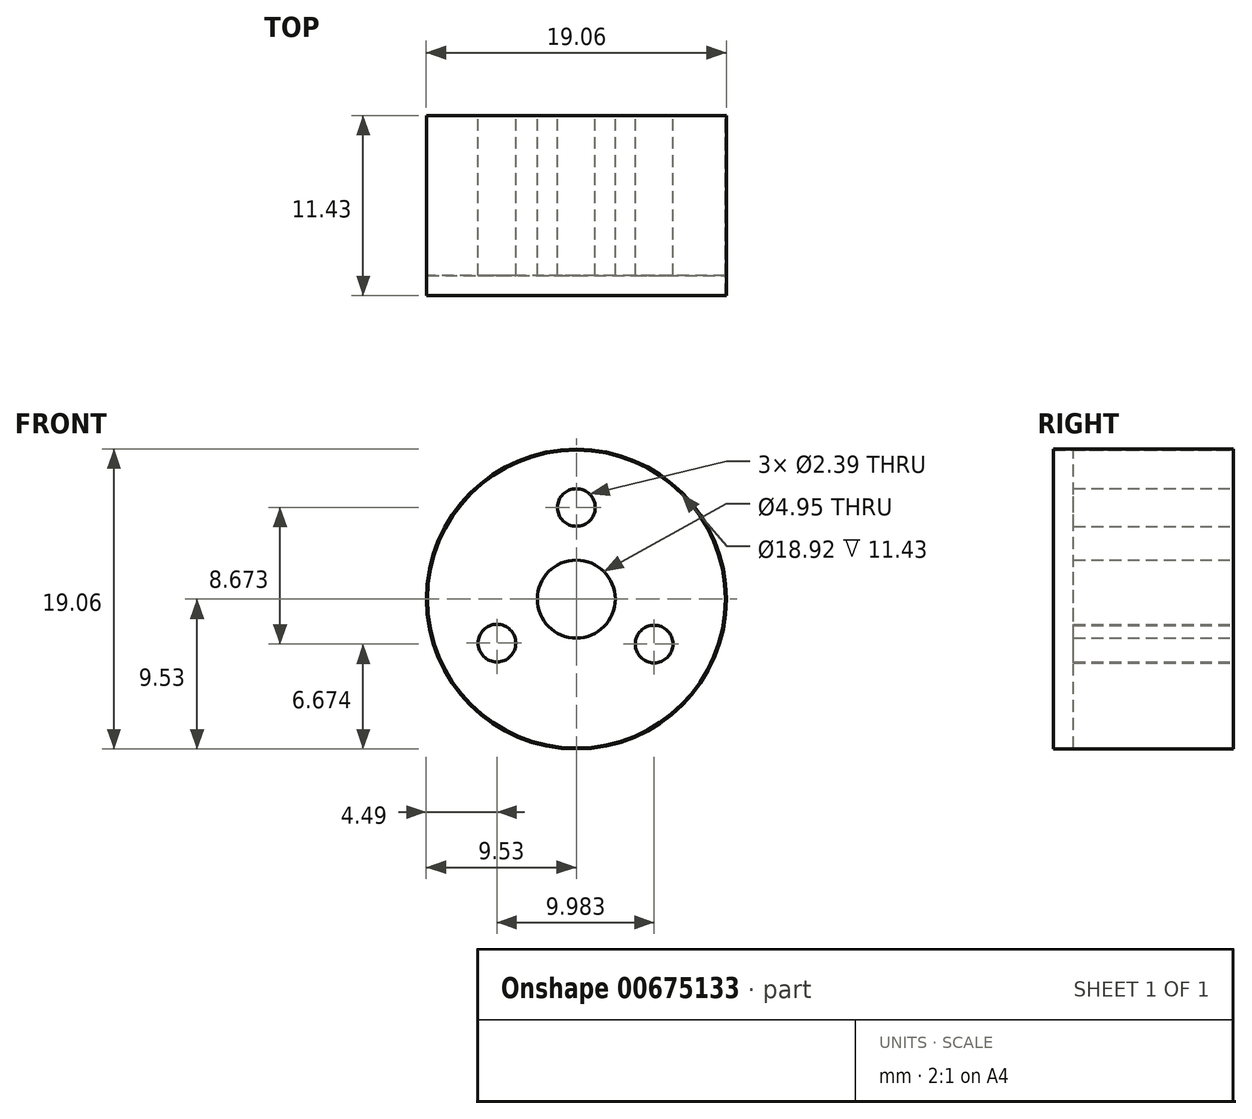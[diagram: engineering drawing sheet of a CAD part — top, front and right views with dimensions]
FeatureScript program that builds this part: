
annotation { "Feature Type Name" : "Feature", "Feature Type Description" : "" }
export const myFeature = defineFeature(function(context is Context, id is Id, definition is map)
    precondition{}
    {
        {
            var Q0;
            Q0=qCreatedBy(makeId("Front.planeOp"),FACE);
            var sketch = newSketch(context, id + "F0", { "sketchPlane" : qUnion([Q0])});
            skEllipse(sketch, "E0", {"center": v(0, 0) * mm, "majorRadius": 9.53 * mm, "minorRadius": 9.53 * mm, "majorAxis": v(0, 1)});
            skCircle(sketch, "E1", {"center": v(0, 0) * mm, "radius": 9.46 * mm});
            skCircle(sketch, "E2", {"center": v(0, 0) * mm, "radius": 2.48 * mm});
            skSolve(sketch);
        }
        {
            var Q0;
            Q0=makeQuery(id+"F0.imprint","IMPRINT",FACE,{"disambiguationData":[TD([[makeQuery(id+"F0.imprint","IMPRINT",EDGE,{"derivedFrom":sQuery(id+"F0.wireOp",EDGE,"E0")}),1.0]])]});
            var sketch = newSketch(context, id + "F1", { "sketchPlane" : qUnion([Q0])});
            skCircle(sketch, "E3", {"center": v(0, 5.82) * mm, "radius": 1.2 * mm});
            skCircle(sketch, "E4.1.0", {"center": v(4.94, -2.86) * mm, "radius": 1.2 * mm});
            skCircle(sketch, "E4.2.0", {"center": v(-5.04, -2.8) * mm, "radius": 1.2 * mm});
            skPoint(sketch, "E4.center", {"position": v(-0.03, 0.05) * mm});
            skLineSegment(sketch, "E4.anchor1", {"start": v(-0.03, 0.05) * mm, "end": v(0, 5.82) * mm, "construction": true});
            skLineSegment(sketch, "E4.anchor2", {"start": v(-0.03, 0.05) * mm, "end": v(-5.04, -2.8) * mm, "construction": true});
            skCircle(sketch, "E5", {"center": v(-10.53, 4.33) * mm, "radius": 0.73 * mm});
            skCircle(sketch, "E6.1.0", {"center": v(1.52, -11.28) * mm, "radius": 0.73 * mm});
            skCircle(sketch, "E6.2.0", {"center": v(9.02, 6.96) * mm, "radius": 0.73 * mm});
            skPoint(sketch, "E6.center", {"position": v(0, 0) * mm});
            skSolve(sketch);
        }
        {
            var Q0;
            Q0=makeQuery(id+"F0.imprint","IMPRINT",FACE,{"disambiguationData":[TD([[makeQuery(id+"F0.imprint","IMPRINT",EDGE,{"derivedFrom":sQuery(id+"F0.wireOp",EDGE,"E1")}),1.0]])]});
            extrude(context, id + "F2", {"entities" : qUnion([Q0]), "depth" : 10.16 * mm, "offsetDistance" : 25.4 * mm});
        }
        {
            var Q0;
            Q0 = qSketchRegion(id + "F0", true);
            extrude(context, id + "F3", {"entities" : qUnion([Q0]), "depth" : 11.43 * mm, "offsetDistance" : 25.4 * mm});
        }
        {
            var Q0;
            Q0 = qSketchRegion(id + "F1", true);
            extrude(context, id + "F4", {"entities" : qUnion([Q0]), "operationType" : NewBodyOperationType.REMOVE, "depth" : 12.32 * mm, "offsetDistance" : 25.4 * mm});
        }
    });
